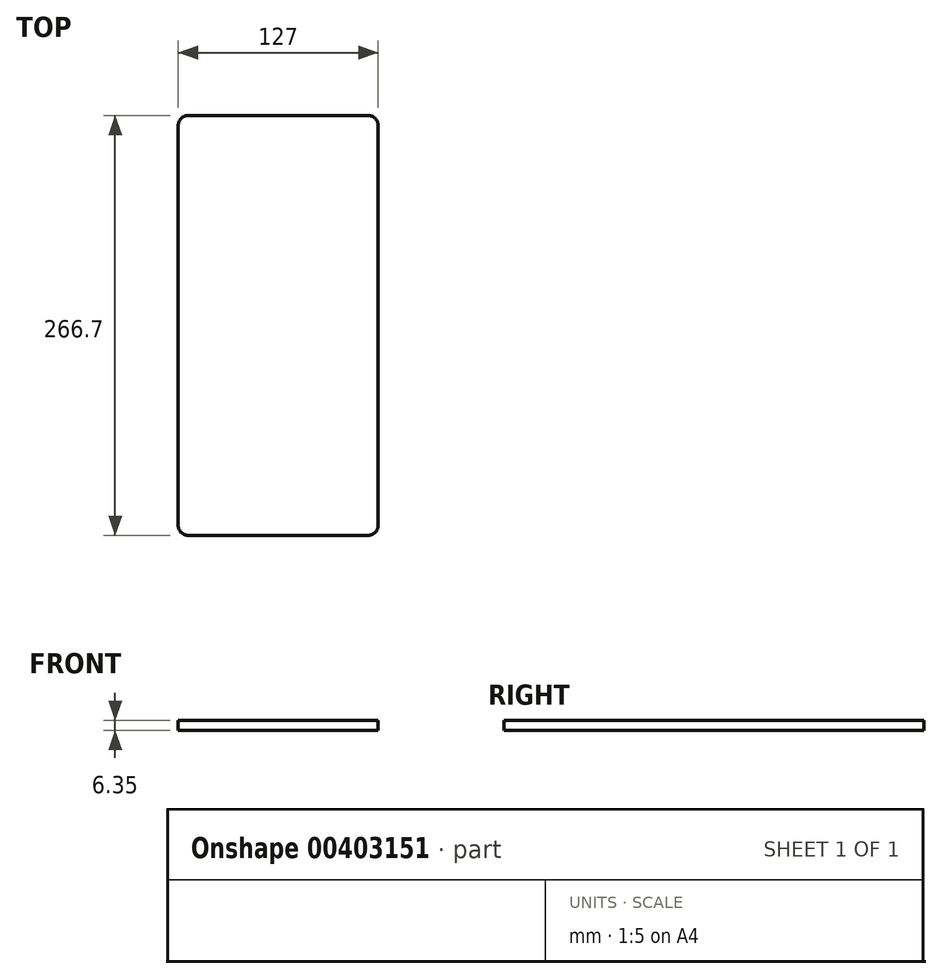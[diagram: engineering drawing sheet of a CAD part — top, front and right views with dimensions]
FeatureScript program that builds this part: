
annotation { "Feature Type Name" : "Feature", "Feature Type Description" : "" }
export const myFeature = defineFeature(function(context is Context, id is Id, definition is map)
    precondition{}
    {
        {
            var Q0;
            Q0=qCreatedBy(makeId("Top.planeOp"),FACE);
            var sketch = newSketch(context, id + "F0", { "sketchPlane" : qUnion([Q0])});
            skLineSegment(sketch, "E0.bottom", {"start": v(57.15, -133.35) * mm, "end": v(-57.15, -133.35) * mm});
            skLineSegment(sketch, "E0.top", {"start": v(57.15, 133.35) * mm, "end": v(-57.15, 133.35) * mm});
            skLineSegment(sketch, "E0.left", {"start": v(63.5, -127) * mm, "end": v(63.5, 127) * mm});
            skLineSegment(sketch, "E0.right", {"start": v(-63.5, -127) * mm, "end": v(-63.5, 127) * mm});
            skPoint(sketch, "E0.middle", {"position": v(0, 0) * mm});
            skPoint(sketch, "E1.visualSharp", {"position": v(-63.5, 133.35) * mm});
            skArc(sketch, "E1.filletArc", {"start": v(-57.15, 133.35) * mm, "mid": v(-61.64, 131.5) * mm, "end": v(-63.5, 127) * mm});
            skPoint(sketch, "E2.visualSharp", {"position": v(-63.5, -133.35) * mm});
            skArc(sketch, "E2.filletArc", {"start": v(-63.5, -127) * mm, "mid": v(-61.64, -131.5) * mm, "end": v(-57.15, -133.35) * mm});
            skPoint(sketch, "E3.visualSharp", {"position": v(63.5, -133.35) * mm});
            skArc(sketch, "E3.filletArc", {"start": v(57.15, -133.35) * mm, "mid": v(61.64, -131.5) * mm, "end": v(63.5, -127) * mm});
            skPoint(sketch, "E4.visualSharp", {"position": v(63.5, 133.35) * mm});
            skArc(sketch, "E4.filletArc", {"start": v(63.5, 127) * mm, "mid": v(61.64, 131.5) * mm, "end": v(57.15, 133.35) * mm});
            skSolve(sketch);
        }
        {
            var Q0;
            Q0=makeQuery(id+"F0.imprint","IMPRINT",FACE,{"disambiguationData":[TD([[makeQuery(id+"F0.imprint","IMPRINT",EDGE,{"derivedFrom":sQuery(id+"F0.wireOp",EDGE,"E0.bottom")}),-1.0]])]});
            extrude(context, id + "F1", {"entities" : qUnion([Q0]), "depth" : 6.35 * mm});
        }
    });
